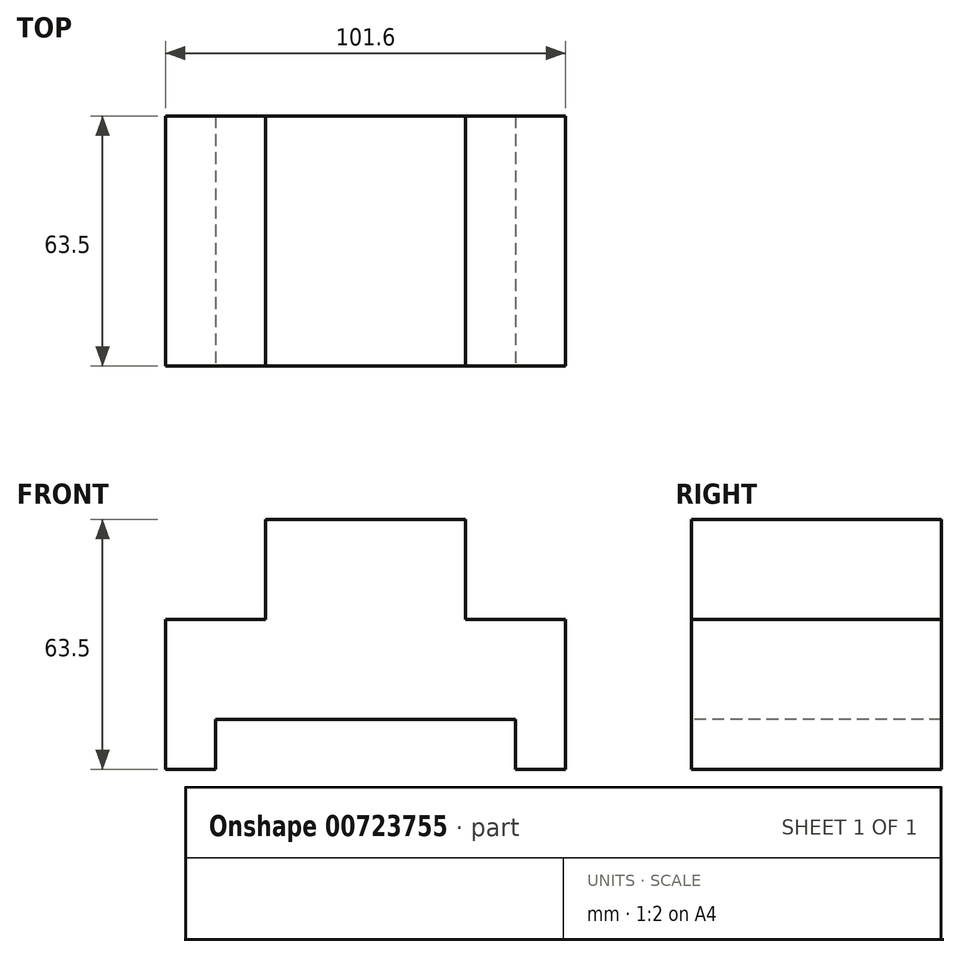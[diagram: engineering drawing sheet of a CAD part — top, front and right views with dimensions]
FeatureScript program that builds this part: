
annotation { "Feature Type Name" : "Feature", "Feature Type Description" : "" }
export const myFeature = defineFeature(function(context is Context, id is Id, definition is map)
    precondition{}
    {
        {
            var Q0;
            Q0=qCreatedBy(makeId("Front.planeOp"),FACE);
            var sketch = newSketch(context, id + "F0", { "sketchPlane" : qUnion([Q0])});
            skLineSegment(sketch, "E0.bottom", {"start": v(0, 0) * mm, "end": v(101.6, 0) * mm});
            skLineSegment(sketch, "E0.top", {"start": v(0, -63.5) * mm, "end": v(101.6, -63.5) * mm});
            skLineSegment(sketch, "E0.left", {"start": v(0, 0) * mm, "end": v(0, -63.5) * mm});
            skLineSegment(sketch, "E0.right", {"start": v(101.6, 0) * mm, "end": v(101.6, -63.5) * mm});
            skSolve(sketch);
        }
        {
            var Q0;
            Q0 = qSketchRegion(id + "F0", true);
            extrude(context, id + "F1", {"entities" : qUnion([Q0]), "depth" : 63.5 * mm, "offsetDistance" : 25.4 * mm});
        }
        {
            var Q0;
            Q0=makeQuery(id+"F1.opExtrude","CAP_FACE",FACE,{"disambiguationData":[OSD([sQuery(id+"F0.wireOp",EDGE,"E0.bottom"),sQuery(id+"F0.wireOp",EDGE,"E0.top"),sQuery(id+"F0.wireOp",EDGE,"E0.left"),sQuery(id+"F0.wireOp",EDGE,"E0.right")])],"isStart":false});
            var sketch = newSketch(context, id + "F2", { "sketchPlane" : qUnion([Q0])});
            skLineSegment(sketch, "E1.bottom", {"start": v(12.7, -63.5) * mm, "end": v(88.9, -63.5) * mm});
            skLineSegment(sketch, "E1.top", {"start": v(12.7, -50.8) * mm, "end": v(88.9, -50.8) * mm});
            skLineSegment(sketch, "E1.left", {"start": v(12.7, -63.5) * mm, "end": v(12.7, -50.8) * mm});
            skLineSegment(sketch, "E1.right", {"start": v(88.9, -63.5) * mm, "end": v(88.9, -50.8) * mm});
            skSolve(sketch);
        }
        {
            var Q0;
            Q0 = qSketchRegion(id + "F2", true);
            extrude(context, id + "F3", {"entities" : qUnion([Q0]), "operationType" : NewBodyOperationType.REMOVE, "oppositeDirection" : true, "depth" : 63.5 * mm, "offsetDistance" : 25.4 * mm});
        }
        {
            var Q0;
            Q0=makeQuery(id+"F1.opExtrude","CAP_FACE",FACE,{"disambiguationData":[OSD([sQuery(id+"F0.wireOp",EDGE,"E0.bottom"),sQuery(id+"F0.wireOp",EDGE,"E0.top"),sQuery(id+"F0.wireOp",EDGE,"E0.left"),sQuery(id+"F0.wireOp",EDGE,"E0.right")])],"isStart":false});
            var sketch = newSketch(context, id + "F4", { "sketchPlane" : qUnion([Q0])});
            skLineSegment(sketch, "E2.bottom", {"start": v(101.6, 0) * mm, "end": v(76.2, 0) * mm});
            skLineSegment(sketch, "E2.top", {"start": v(101.6, -25.4) * mm, "end": v(76.2, -25.4) * mm});
            skLineSegment(sketch, "E2.left", {"start": v(101.6, 0) * mm, "end": v(101.6, -25.4) * mm});
            skLineSegment(sketch, "E2.right", {"start": v(76.2, 0) * mm, "end": v(76.2, -25.4) * mm});
            skSolve(sketch);
        }
        {
            var Q0;
            Q0 = qSketchRegion(id + "F4", true);
            extrude(context, id + "F5", {"entities" : qUnion([Q0]), "operationType" : NewBodyOperationType.REMOVE, "oppositeDirection" : true, "depth" : 63.5 * mm, "offsetDistance" : 25.4 * mm});
        }
        {
            var Q0;
            Q0=makeQuery(id+"F1.opExtrude","CAP_FACE",FACE,{"disambiguationData":[OSD([sQuery(id+"F0.wireOp",EDGE,"E0.bottom"),sQuery(id+"F0.wireOp",EDGE,"E0.top"),sQuery(id+"F0.wireOp",EDGE,"E0.left"),sQuery(id+"F0.wireOp",EDGE,"E0.right")])],"isStart":false});
            var sketch = newSketch(context, id + "F6", { "sketchPlane" : qUnion([Q0])});
            skLineSegment(sketch, "E3.bottom", {"start": v(0, 0) * mm, "end": v(25.4, 0) * mm});
            skLineSegment(sketch, "E3.top", {"start": v(0, -25.4) * mm, "end": v(25.4, -25.4) * mm});
            skLineSegment(sketch, "E3.left", {"start": v(0, 0) * mm, "end": v(0, -25.4) * mm});
            skLineSegment(sketch, "E3.right", {"start": v(25.4, 0) * mm, "end": v(25.4, -25.4) * mm});
            skSolve(sketch);
        }
        {
            var Q0;
            Q0 = qSketchRegion(id + "F6", true);
            extrude(context, id + "F7", {"entities" : qUnion([Q0]), "operationType" : NewBodyOperationType.REMOVE, "oppositeDirection" : true, "depth" : 63.5 * mm, "offsetDistance" : 25.4 * mm});
        }
    });
